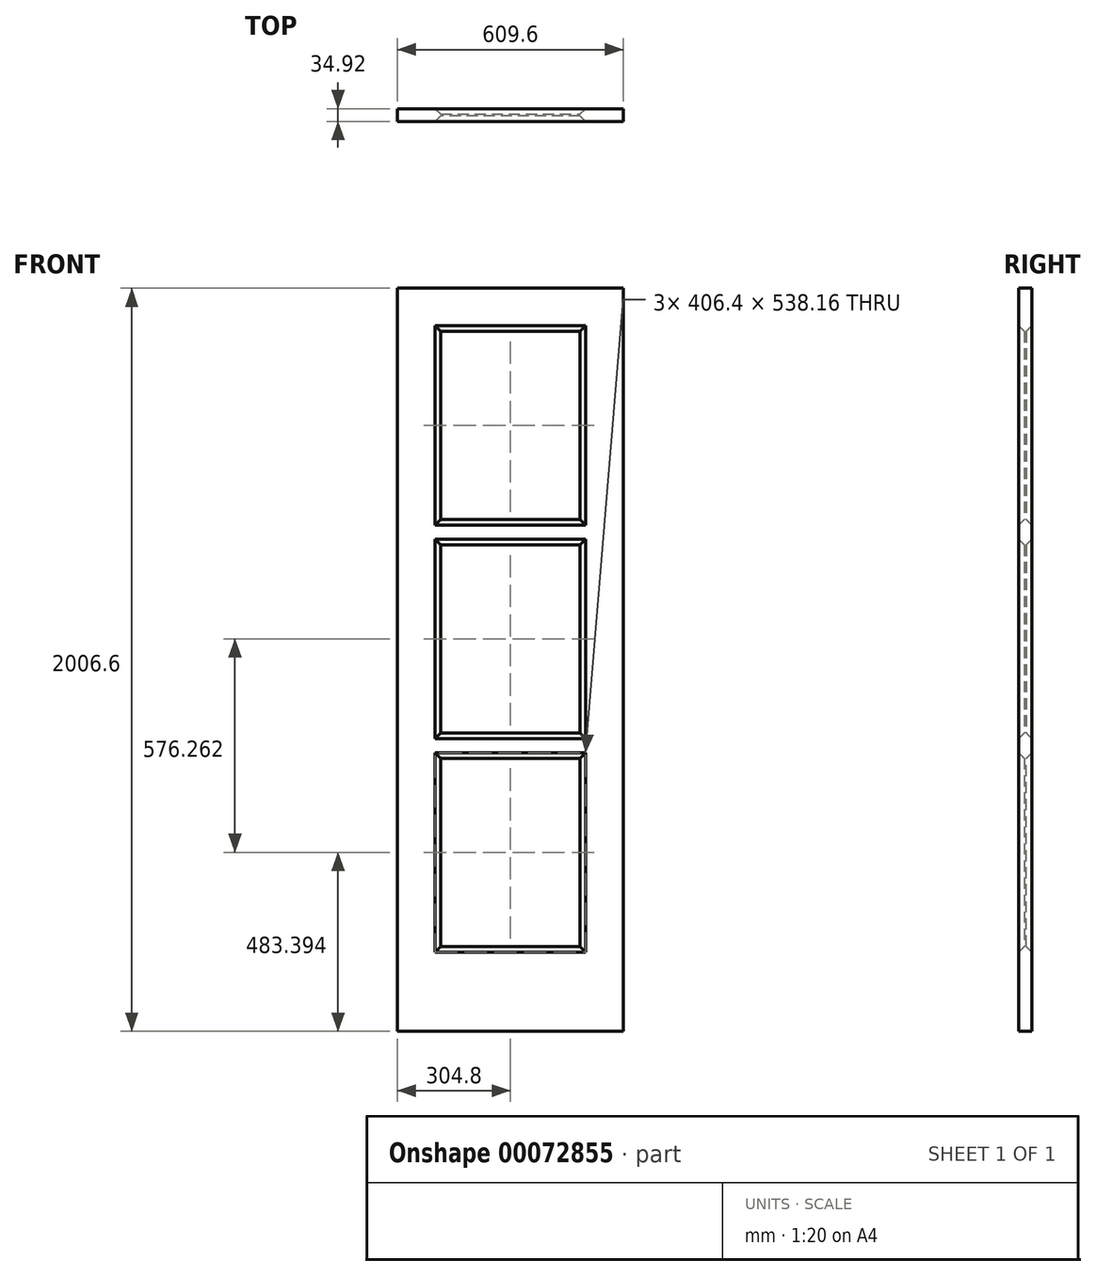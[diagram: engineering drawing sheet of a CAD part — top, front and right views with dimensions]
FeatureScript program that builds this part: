
annotation { "Feature Type Name" : "Feature", "Feature Type Description" : "" }
export const myFeature = defineFeature(function(context is Context, id is Id, definition is map)
    precondition{}
    {
        {
            var Q0;
            Q0=qCreatedBy(makeId("Front.planeOp"),FACE);
            var sketch = newSketch(context, id + "F0", { "sketchPlane" : qUnion([Q0])});
            skLineSegment(sketch, "E0.bottom", {"start": v(-304.8, 2006.6) * mm, "end": v(304.8, 2006.6) * mm});
            skLineSegment(sketch, "E0.top", {"start": v(-304.8, 0) * mm, "end": v(304.8, 0) * mm});
            skLineSegment(sketch, "E0.left", {"start": v(-304.8, 2006.6) * mm, "end": v(-304.8, 0) * mm});
            skLineSegment(sketch, "E0.right", {"start": v(304.8, 2006.6) * mm, "end": v(304.8, 0) * mm});
            skLineSegment(sketch, "E1", {"start": v(0, 0) * mm, "end": v(0, 2006.6) * mm, "construction": true});
            skLineSegment(sketch, "E2.bottom", {"start": v(-203.2, 1905) * mm, "end": v(203.2, 1905) * mm});
            skLineSegment(sketch, "E2.top", {"start": v(-203.2, 1366.84) * mm, "end": v(203.2, 1366.84) * mm});
            skLineSegment(sketch, "E2.left", {"start": v(-203.2, 1905) * mm, "end": v(-203.2, 1366.84) * mm});
            skLineSegment(sketch, "E2.right", {"start": v(203.2, 1905) * mm, "end": v(203.2, 1366.84) * mm});
            skLineSegment(sketch, "E3.bottom", {"start": v(-203.2, 1328.74) * mm, "end": v(203.2, 1328.74) * mm});
            skLineSegment(sketch, "E3.top", {"start": v(-203.2, 790.58) * mm, "end": v(203.2, 790.58) * mm});
            skLineSegment(sketch, "E3.left", {"start": v(-203.2, 1328.74) * mm, "end": v(-203.2, 790.58) * mm});
            skLineSegment(sketch, "E3.right", {"start": v(203.2, 1328.74) * mm, "end": v(203.2, 790.58) * mm});
            skLineSegment(sketch, "E4.bottom", {"start": v(-203.2, 752.48) * mm, "end": v(203.2, 752.48) * mm});
            skLineSegment(sketch, "E4.top", {"start": v(-203.2, 214.31) * mm, "end": v(203.2, 214.31) * mm});
            skLineSegment(sketch, "E4.left", {"start": v(-203.2, 752.48) * mm, "end": v(-203.2, 214.31) * mm});
            skLineSegment(sketch, "E4.right", {"start": v(203.2, 752.48) * mm, "end": v(203.2, 214.31) * mm});
            skSolve(sketch);
        }
        {
            var Q0;
            Q0=makeQuery(id+"F0.imprint","IMPRINT",FACE,{"disambiguationData":[TD([[makeQuery(id+"F0.imprint","IMPRINT",EDGE,{"derivedFrom":sQuery(id+"F0.wireOp",EDGE,"E4.bottom")}),-1.0]])]});
            var Q1;
            Q1=makeQuery(id+"F0.imprint","IMPRINT",FACE,{"disambiguationData":[TD([[makeQuery(id+"F0.imprint","IMPRINT",EDGE,{"derivedFrom":sQuery(id+"F0.wireOp",EDGE,"E3.bottom")}),-1.0]])]});
            var Q2;
            Q2=makeQuery(id+"F0.imprint","IMPRINT",FACE,{"disambiguationData":[TD([[makeQuery(id+"F0.imprint","IMPRINT",EDGE,{"derivedFrom":sQuery(id+"F0.wireOp",EDGE,"E2.bottom")}),-1.0]])]});
            var Q3;
            Q3=makeQuery(id+"F0.imprint","IMPRINT",FACE,{"disambiguationData":[TD([[makeQuery(id+"F0.imprint","IMPRINT",EDGE,{"derivedFrom":sQuery(id+"F0.wireOp",EDGE,"E0.bottom")}),-1.0]])]});
            extrude(context, id + "F1", {"entities" : qUnion([Q0, Q1, Q2, Q3]), "endBound" : BoundingType.SYMMETRIC, "depth" : 34.92 * mm});
        }
        {
            var Q0;
            Q0=makeQuery(id+"F1.opExtrude","CAP_FACE",FACE,{"disambiguationData":[OSD([sQuery(id+"F0.wireOp",EDGE,"E0.bottom"),sQuery(id+"F0.wireOp",EDGE,"E0.top"),sQuery(id+"F0.wireOp",EDGE,"E0.left"),sQuery(id+"F0.wireOp",EDGE,"E0.right")])],"isStart":true});
            var sketch = newSketch(context, id + "F2", { "sketchPlane" : qUnion([Q0])});
            skLineSegment(sketch, "E5.0", {"start": v(-203.2, 1905) * mm, "end": v(-203.2, 1366.84) * mm});
            skLineSegment(sketch, "E6.0", {"start": v(203.2, 1905) * mm, "end": v(-203.2, 1905) * mm});
            skLineSegment(sketch, "E7.0", {"start": v(203.2, 1905) * mm, "end": v(203.2, 1366.84) * mm});
            skLineSegment(sketch, "E8.0", {"start": v(203.2, 1366.84) * mm, "end": v(-203.2, 1366.84) * mm});
            skLineSegment(sketch, "E9.0", {"start": v(-203.2, 1328.74) * mm, "end": v(-203.2, 790.58) * mm});
            skLineSegment(sketch, "E10.0", {"start": v(203.2, 1328.74) * mm, "end": v(-203.2, 1328.74) * mm});
            skLineSegment(sketch, "E11.0", {"start": v(203.2, 1328.74) * mm, "end": v(203.2, 790.58) * mm});
            skLineSegment(sketch, "E12.0", {"start": v(203.2, 790.58) * mm, "end": v(-203.2, 790.58) * mm});
            skLineSegment(sketch, "E13.0", {"start": v(203.2, 752.48) * mm, "end": v(-203.2, 752.48) * mm});
            skLineSegment(sketch, "E14.0", {"start": v(203.2, 752.48) * mm, "end": v(203.2, 214.31) * mm});
            skLineSegment(sketch, "E15.0", {"start": v(203.2, 214.31) * mm, "end": v(-203.2, 214.31) * mm});
            skLineSegment(sketch, "E16.0", {"start": v(-203.2, 752.48) * mm, "end": v(-203.2, 214.31) * mm});
            skSolve(sketch);
        }
        {
            var Q0;
            Q0=qSketchRegion(id+"F2",true);
            extrude(context, id + "F3", {"entities" : qUnion([Q0]), "operationType" : NewBodyOperationType.REMOVE, "oppositeDirection" : true, "depth" : 15.08 * mm, "hasDraft" : true, "draftAngle" : 45 * degree, "draftPullDirection" : true});
        }
        {
            var Q0;
            Q0=makeQuery(id+"F1.opExtrude","CAP_FACE",FACE,{"disambiguationData":[OSD([sQuery(id+"F0.wireOp",EDGE,"E0.bottom"),sQuery(id+"F0.wireOp",EDGE,"E0.top"),sQuery(id+"F0.wireOp",EDGE,"E0.left"),sQuery(id+"F0.wireOp",EDGE,"E0.right")])],"isStart":false});
            var sketch = newSketch(context, id + "F4", { "sketchPlane" : qUnion([Q0])});
            skLineSegment(sketch, "E17.0", {"start": v(-203.2, 1905) * mm, "end": v(-203.2, 1366.84) * mm});
            skLineSegment(sketch, "E18.0", {"start": v(-203.2, 1905) * mm, "end": v(203.2, 1905) * mm});
            skLineSegment(sketch, "E19.0", {"start": v(203.2, 1905) * mm, "end": v(203.2, 1366.84) * mm});
            skLineSegment(sketch, "E20.0", {"start": v(-203.2, 1366.84) * mm, "end": v(203.2, 1366.84) * mm});
            skLineSegment(sketch, "E21.0", {"start": v(-203.2, 1328.74) * mm, "end": v(203.2, 1328.74) * mm});
            skLineSegment(sketch, "E22.0", {"start": v(-203.2, 1328.74) * mm, "end": v(-203.2, 790.58) * mm});
            skLineSegment(sketch, "E23.0", {"start": v(203.2, 1328.74) * mm, "end": v(203.2, 790.58) * mm});
            skLineSegment(sketch, "E24.0", {"start": v(-203.2, 790.58) * mm, "end": v(203.2, 790.58) * mm});
            skLineSegment(sketch, "E25.0", {"start": v(-203.2, 752.48) * mm, "end": v(203.2, 752.48) * mm});
            skLineSegment(sketch, "E26.0", {"start": v(203.2, 752.48) * mm, "end": v(203.2, 214.31) * mm});
            skLineSegment(sketch, "E27.0", {"start": v(-203.2, 752.48) * mm, "end": v(-203.2, 214.31) * mm});
            skLineSegment(sketch, "E28.0", {"start": v(-203.2, 214.31) * mm, "end": v(203.2, 214.31) * mm});
            skSolve(sketch);
        }
        {
            var Q0;
            Q0=qSketchRegion(id+"F4",true);
            extrude(context, id + "F5", {"entities" : qUnion([Q0]), "operationType" : NewBodyOperationType.REMOVE, "oppositeDirection" : true, "depth" : 15.08 * mm, "hasDraft" : true, "draftAngle" : 45 * degree, "draftPullDirection" : true});
        }
    });
